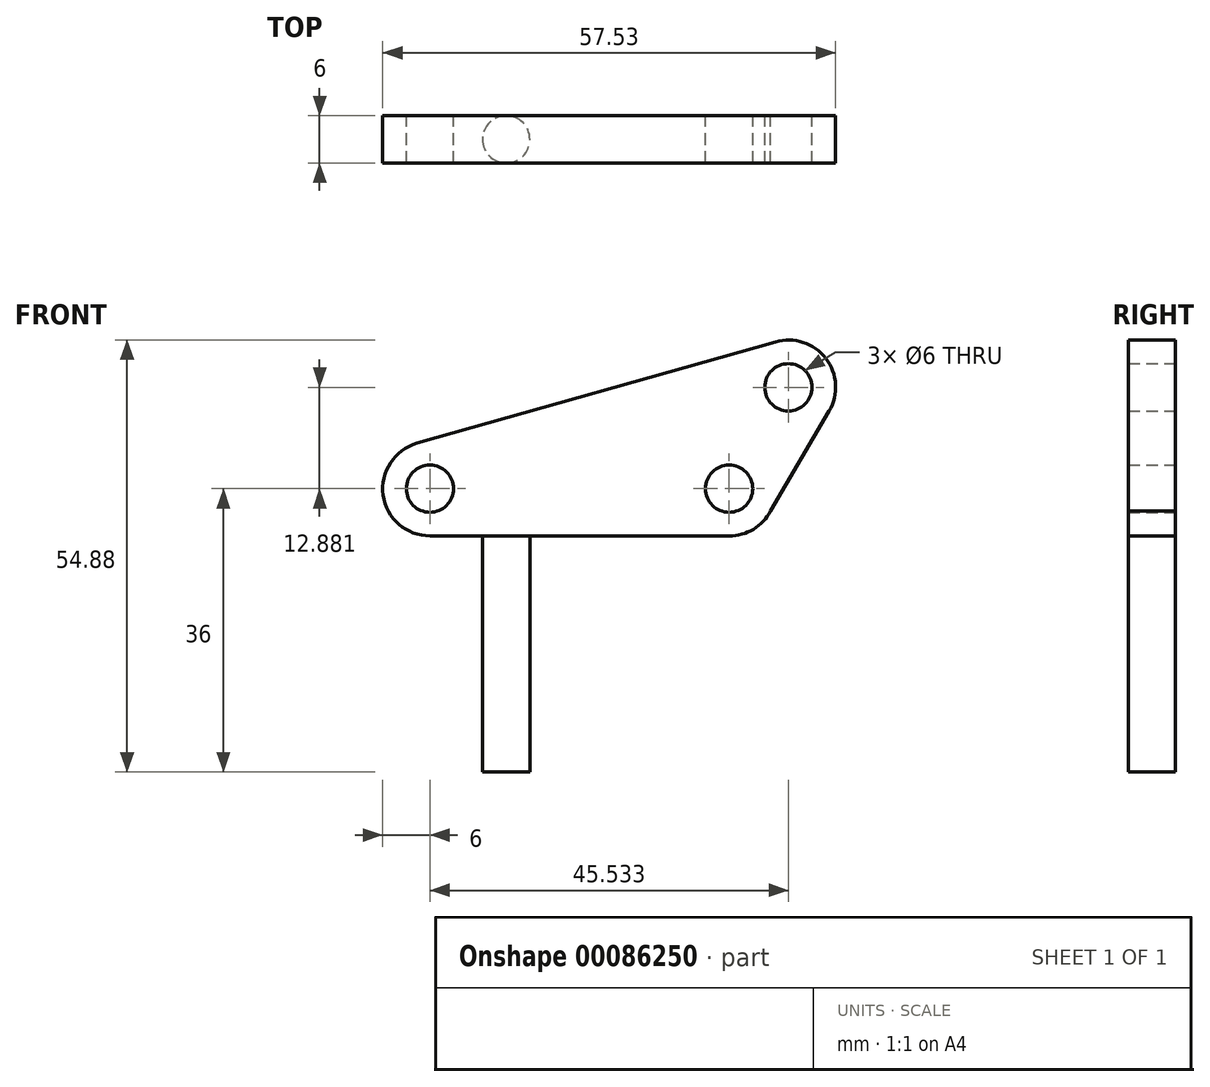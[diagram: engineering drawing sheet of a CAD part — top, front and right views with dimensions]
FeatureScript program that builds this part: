
annotation { "Feature Type Name" : "Feature", "Feature Type Description" : "" }
export const myFeature = defineFeature(function(context is Context, id is Id, definition is map)
    precondition{}
    {
        {
            var Q0;
            Q0=qCreatedBy(makeId("Front.planeOp"),FACE);
            var sketch = newSketch(context, id + "F0", { "sketchPlane" : qUnion([Q0])});
            skCircle(sketch, "E0", {"center": v(0, 0) * mm, "radius": 3 * mm});
            skCircle(sketch, "E1", {"center": v(38, 0) * mm, "radius": 3 * mm});
            skCircle(sketch, "E2", {"center": v(45.53, 12.88) * mm, "radius": 3 * mm});
            skArc(sketch, "E3", {"start": v(-1.63, 5.77) * mm, "mid": v(-5.94, -0.82) * mm, "end": v(0, -6) * mm});
            skArc(sketch, "E4", {"start": v(38, -6) * mm, "mid": v(41.07, -5.16) * mm, "end": v(43.28, -2.86) * mm});
            skArc(sketch, "E5", {"start": v(50.71, 9.85) * mm, "mid": v(50.28, 16.55) * mm, "end": v(43.9, 18.65) * mm});
            skLineSegment(sketch, "E6", {"start": v(0, -6) * mm, "end": v(38, -6) * mm});
            skLineSegment(sketch, "E7", {"start": v(-1.63, 5.77) * mm, "end": v(43.9, 18.65) * mm});
            skLineSegment(sketch, "E8", {"start": v(50.71, 9.85) * mm, "end": v(43.28, -2.86) * mm});
            skSolve(sketch);
        }
        {
            var Q0;
            Q0=makeQuery(id+"F0.imprint","IMPRINT",FACE,{"disambiguationData":[TD([[makeQuery(id+"F0.imprint","IMPRINT",EDGE,{"derivedFrom":sQuery(id+"F0.wireOp",EDGE,"E0")}),-1.0]])]});
            extrude(context, id + "F1", {"entities" : qUnion([Q0]), "depth" : 6 * mm});
        }
        {
            var Q0;
            Q0=makeQuery(id+"F1.opExtrude","SWEPT_FACE",FACE,{"disambiguationData":[OSD([sQuery(id+"F0.wireOp",EDGE,"E6")])]});
            var sketch = newSketch(context, id + "F2", { "sketchPlane" : qUnion([Q0])});
            skPoint(sketch, "E9.endSnap0", {"position": v(38, 3) * mm});
            skCircle(sketch, "E10", {"center": v(9.68, 3) * mm, "radius": 3 * mm});
            skLineSegment(sketch, "E11.trimOffspring", {"start": v(38, 3) * mm, "end": v(38.68, 3) * mm});
            skPoint(sketch, "E12.orphan", {"position": v(9.68, 0) * mm});
            skPoint(sketch, "E13.end.orphan", {"position": v(9.68, 6) * mm});
            skPoint(sketch, "E9.start.orphan", {"position": v(0, 3) * mm});
            skSolve(sketch);
        }
        {
            var Q0;
            {var subQ0=sQuery(id+"F2.wireOp",EDGE,"E10");var subQ1=sQuery(id+"F0.wireOp",EDGE,"E6");var subQ2=makeQuery(id+"F2.imprint","INTERSECT",VERTEX,{"derivedFrom":[makeQuery(id+"F1.opExtrude","CAP_EDGE",EDGE,{"disambiguationData":[OSD([subQ1])],"isStart":true}),subQ0]});Q0=makeQuery(id+"F2.imprint","IMPRINT",FACE,{"disambiguationData":[TD([[makeQuery(id+"F2.imprint","IMPRINT",EDGE,{"disambiguationData":[TD([[subQ2,1.0]])],"derivedFrom":subQ0}),1.0]])]});}
            extrude(context, id + "F3", {"entities" : qUnion([Q0]), "operationType" : NewBodyOperationType.ADD, "depth" : 30 * mm});
        }
    });
